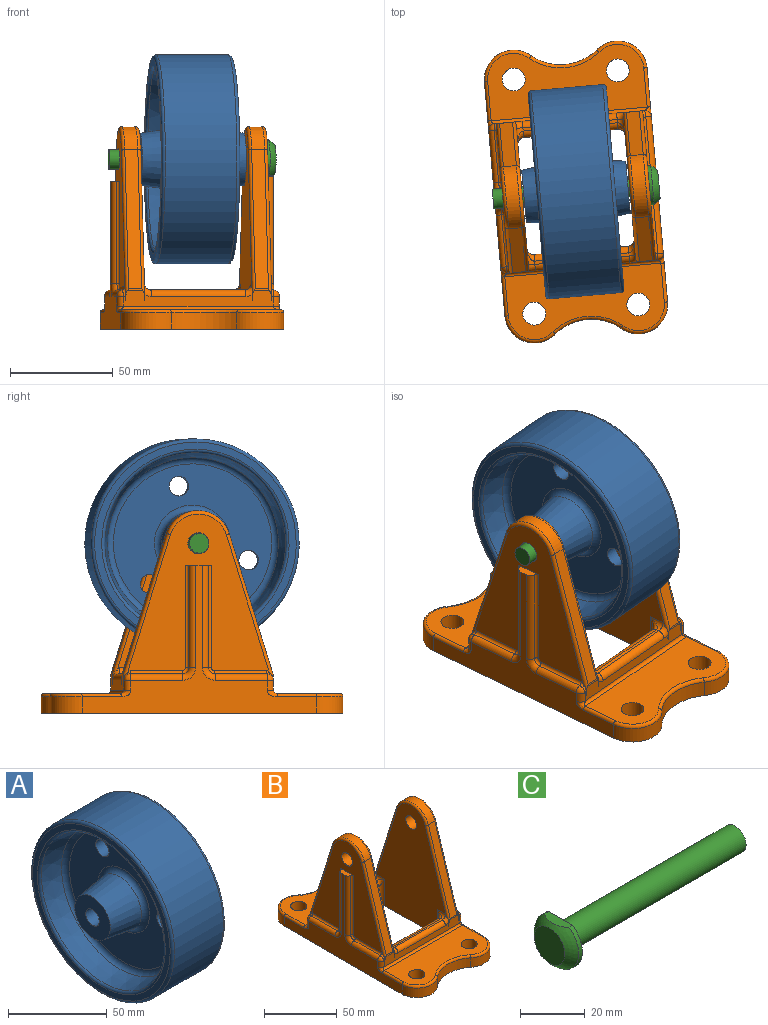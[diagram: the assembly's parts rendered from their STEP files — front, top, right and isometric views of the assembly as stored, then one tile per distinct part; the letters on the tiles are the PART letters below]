
ASSEMBLY  parts=3 mates=2
PART A: 23 faces, bbox 50.8x110x110 mm
  f0: cone r=15.49mm half-angle=8.1deg, axis (-1,0,0), area 1744.1mm2, adj f1,f19
  f1: torus R=18.63mm, axis (1,0,0), area 476.6mm2, adj f0,f2
  f2: plane 77.34x77.34mm, normal (1,0,0), area 3394.4mm2, adj f1,f3,f20,f21,f22
  f3: torus R=38.67mm, axis (1,0,0), area 1110.5mm2, adj f2,f4
  f4: cone r=44.19mm half-angle=11.3deg, axis (1,0,0), area 3318.4mm2, adj f3,f5
  f5: torus R=45.75mm, axis (1,0,0), area 614mm2, adj f4,f6
  f6: plane 98.43x98.43mm, normal (1,0,0), area 1032.6mm2, adj f5,f7
  f7: torus R=49.21mm, axis (1,0,0), area 786.9mm2, adj f6,f8
  f8: cylinder r=50.8mm len=101.6mm, axis (1,0,0), area 11147.6mm2, adj f7,f9
  f9: torus R=49.21mm, axis (1,0,0), area 786.9mm2, adj f8,f10
  f10: plane 98.43x98.43mm, normal (-1,0,0), area 1032.6mm2, adj f9,f11
  f11: torus R=45.75mm, axis (1,0,0), area 614mm2, adj f10,f12
  f12: cone r=44.19mm half-angle=11.3deg, axis (-1,0,0), area 3318.4mm2, adj f11,f13
  f13: torus R=38.67mm, axis (1,0,0), area 1110.5mm2, adj f12,f14
  f14: plane 77.34x77.34mm, normal (-1,0,0), area 3394.4mm2, adj f13,f15,f20,f21,f22
  f15: torus R=18.63mm, axis (1,0,0), area 476.6mm2, adj f14,f16
  f16: cone r=15.49mm half-angle=8.1deg, axis (1,0,0), area 1744.1mm2, adj f15,f17
  f17: plane 25.4x25.4mm, normal (-1,0,0), area 433.5mm2, adj f16,f18
  f18: cylinder r=4.83mm len=50.8mm, axis (1,0,0), area 1540.4mm2, adj f17,f19
  f19: plane 25.4x25.4mm, normal (1,0,0), area 433.5mm2, adj f0,f18
  f20: cylinder r=4.76mm len=9.53mm, axis (-1,0,0), area 190mm2, adj f2,f14
  f21: cylinder r=4.76mm len=9.53mm, axis (-1,0,0), area 190mm2, adj f2,f14
  f22: cylinder r=4.76mm len=9.53mm, axis (-1,0,0), area 190mm2, adj f2,f14
PART B: 131 faces, bbox 82.6x146.1x100.6 mm
  f0: cylinder r=1.59mm len=49.76mm, axis (0,0,-1), area 110.8mm2, adj f24,f89,f101,f130
  f1: cylinder r=1.59mm len=49.76mm, axis (0,0,1), area 110.8mm2, adj f24,f91,f102,f130
  f2: plane 114.87x72.55mm, normal (-1,0,0), area 1649.1mm2, adj f10,f16,f18,f50,f56,f99,f100,f101
  f3: plane 114.87x74.94mm, normal (1,0,0), area 1657mm2, adj f10,f12,f22,f52,f59,f81,f96,f97
  f4: plane 76.21x68.34mm, normal (1,0,0), area 2608.7mm2, adj f43,f44,f45,f46,f81,f86,f87,f88
  f5: plane 7.72x2.42mm, normal (1,0,0), area 5.4mm2, adj f8,f49,f127
  f6: plane 7.72x2.42mm, normal (-1,0,0), area 5.4mm2, adj f8,f32,f129
  f7: plane 46.04x15.88mm, normal (0,-1,0), area 730.8mm2, adj f10,f61,f66,f73
  f8: plane 73.91x8.33mm, normal (0,1,0), area 396mm2, adj f5,f6,f32,f35,f46,f49,f76,f78
  f9: plane 46.04x1.59mm, normal (0,0,1), area 73.1mm2, adj f62,f65,f73,f128
  f10: plane 142.88x79.38mm, normal (0,0,-1), area 7276.6mm2, adj f2,f3,f7,f11,f12,f13,f14,f15
  f11: plane 96.84x67.46mm, normal (-1,0,0), area 4313.3mm2, adj f10,f43,f47,f48,f49,f61,f62,f67
  f12: cylinder r=14.29mm len=23.7mm, axis (0,0,-1), area 259.7mm2, adj f3,f10,f13,f21
  f13: cylinder r=25.4mm len=31.97mm, axis (0,0,-1), area 274.4mm2, adj f10,f12,f16,f20
  f14: cylinder r=5.56mm len=11.11mm, axis (0,0,-1), area 332.5mm2, adj f10,f17
  f15: cylinder r=5.56mm len=11.11mm, axis (0,0,-1), area 332.5mm2, adj f10,f17
  f16: cylinder r=14.29mm len=23.7mm, axis (0,0,-1), area 259.7mm2, adj f2,f10,f13,f19
  f17: plane 76.2x31.75mm, normal (0,0,1), area 1891.4mm2, adj f14,f15,f18,f19,f20,f21,f22,f85
  f18: cylinder r=1.59mm len=19.05mm, axis (0,1,0), area 47.5mm2, adj f2,f17,f19,f111
  f19: torus R=12.7mm, axis (0,0,1), area 78.3mm2, adj f16,f17,f18,f20
  f20: torus R=26.99mm, axis (0,0,1), area 88.3mm2, adj f13,f17,f19,f21
  f21: torus R=12.7mm, axis (0,0,1), area 78.3mm2, adj f12,f17,f20,f22
  f22: cylinder r=1.59mm len=19.05mm, axis (0,-1,0), area 47.5mm2, adj f3,f17,f21,f123
  f23: plane 96.84x67.46mm, normal (1,0,0), area 4313.3mm2, adj f10,f29,f30,f31,f32,f63,f64,f65
  f24: plane 76.21x68.34mm, normal (-1,0,0), area 2639mm2, adj f0,f1,f29,f33,f34,f35,f89,f90
  f25: plane 73.91x8.33mm, normal (0,-1,0), area 396mm2, adj f30,f33,f36,f37,f44,f47,f75,f77
  f26: plane 67.78x21.22mm, normal (0,-0.95,0.3), area 451mm2, adj f27,f30,f33,f75
  f27: cylinder r=15.88mm len=30.3mm, axis (-1,0,0), area 255.5mm2, adj f26,f28,f31,f34
  f28: plane 67.78x21.22mm, normal (0,0.95,0.3), area 451mm2, adj f27,f32,f35,f76
  f29: cylinder r=5.16mm len=10.32mm, axis (-1,0,0), area 308.8mm2, adj f23,f24
  f30: cylinder r=1.59mm len=73.62mm, axis (0,-0.3,-0.95), area 183.5mm2, adj f23,f25,f26,f31,f37,f75,f126
  f31: torus R=14.29mm, axis (-1,0,0), area 96.7mm2, adj f23,f27,f30,f32
  f32: cylinder r=1.59mm len=73.62mm, axis (0,-0.3,0.95), area 183.5mm2, adj f6,f8,f23,f28,f31,f76,f129
  f33: cylinder r=1.59mm len=73.68mm, axis (0,-0.3,-0.95), area 183.8mm2, adj f24,f25,f26,f34,f75,f83,f116
  f34: torus R=14.29mm, axis (1,0,0), area 96.7mm2, adj f24,f27,f33,f35
  f35: cylinder r=1.59mm len=73.68mm, axis (0,-0.3,0.95), area 183.8mm2, adj f8,f24,f28,f34,f76,f82,f108
  f36: plane 7.72x2.42mm, normal (1,0,0), area 5.4mm2, adj f25,f47,f124
  f37: plane 7.72x2.42mm, normal (-1,0,0), area 5.4mm2, adj f25,f30,f126
  f38: plane 46.04x15.88mm, normal (0,1,0), area 730.8mm2, adj f10,f63,f68,f70
  f39: plane 46.04x1.59mm, normal (0,0,1), area 73.1mm2, adj f64,f67,f70,f125
  f40: plane 67.78x21.22mm, normal (0,-0.95,0.3), area 451mm2, adj f41,f44,f47,f77
  f41: cylinder r=15.88mm len=30.3mm, axis (-1,0,0), area 255.5mm2, adj f40,f42,f45,f48
  f42: plane 67.78x21.22mm, normal (0,0.95,0.3), area 451mm2, adj f41,f46,f49,f78
  f43: cylinder r=5.16mm len=10.32mm, axis (-1,0,0), area 308.8mm2, adj f4,f11
  f44: cylinder r=1.59mm len=73.68mm, axis (0,-0.3,-0.95), area 183.8mm2, adj f4,f25,f40,f45,f77,f80,f112
  f45: torus R=14.29mm, axis (-1,0,0), area 96.7mm2, adj f4,f41,f44,f46
  f46: cylinder r=1.59mm len=73.68mm, axis (0,-0.3,0.95), area 183.8mm2, adj f4,f8,f42,f45,f78,f79,f120
  f47: cylinder r=1.59mm len=73.62mm, axis (0,0.3,0.95), area 183.5mm2, adj f11,f25,f36,f40,f48,f77,f124
  f48: torus R=14.29mm, axis (1,0,0), area 96.7mm2, adj f11,f41,f47,f49
  f49: cylinder r=1.59mm len=73.62mm, axis (0,0.3,-0.95), area 183.5mm2, adj f5,f8,f11,f42,f48,f78,f127
  f50: cylinder r=14.29mm len=23.7mm, axis (0,0,-1), area 259.7mm2, adj f2,f10,f51,f57
  f51: cylinder r=25.4mm len=31.97mm, axis (0,0,-1), area 274.4mm2, adj f10,f50,f52,f58
  f52: cylinder r=14.29mm len=23.7mm, axis (0,0,-1), area 259.7mm2, adj f3,f10,f51,f60
  f53: cylinder r=5.56mm len=11.11mm, axis (0,0,-1), area 332.5mm2, adj f10,f55
  f54: cylinder r=5.56mm len=11.11mm, axis (0,0,-1), area 332.5mm2, adj f10,f55
  f55: plane 76.2x31.75mm, normal (0,0,1), area 1891.4mm2, adj f53,f54,f56,f57,f58,f59,f60,f84
  f56: cylinder r=1.59mm len=19.05mm, axis (0,1,0), area 47.5mm2, adj f2,f55,f57,f119
  f57: torus R=12.7mm, axis (0,0,1), area 78.3mm2, adj f50,f55,f56,f58
  f58: torus R=26.99mm, axis (0,0,1), area 88.3mm2, adj f51,f55,f57,f60
  f59: cylinder r=1.59mm len=19.05mm, axis (0,-1,0), area 47.5mm2, adj f3,f55,f60,f115
  f60: torus R=12.7mm, axis (0,0,1), area 78.3mm2, adj f52,f55,f58,f59
  f61: cylinder r=3.17mm len=22.23mm, axis (0,0,-1), area 95mm2, adj f7,f10,f11,f74
  f62: cylinder r=3.17mm len=7.94mm, axis (0,-1,0), area 19.4mm2, adj f9,f11,f74,f127
  f63: cylinder r=3.17mm len=22.23mm, axis (0,0,1), area 95mm2, adj f10,f23,f38,f69
  f64: cylinder r=3.17mm len=7.94mm, axis (0,1,0), area 19.4mm2, adj f23,f39,f69,f126
  f65: cylinder r=3.17mm len=7.94mm, axis (0,1,0), area 19.4mm2, adj f9,f23,f72,f129
  f66: cylinder r=3.17mm len=22.23mm, axis (0,0,-1), area 95mm2, adj f7,f10,f23,f72
  f67: cylinder r=3.17mm len=7.94mm, axis (0,-1,0), area 19.4mm2, adj f11,f39,f71,f124
  f68: cylinder r=3.17mm len=22.23mm, axis (0,0,1), area 95mm2, adj f10,f11,f38,f71
  f69: bspline ~6.35x6.35mm, area 10.6mm2, adj f63,f64,f70
  f70: cylinder r=3.17mm len=46.04mm, axis (1,0,0), area 229.6mm2, adj f38,f39,f69,f71
  f71: bspline ~6.35x6.35mm, area 10.6mm2, adj f67,f68,f70
  f72: bspline ~6.35x6.35mm, area 10.6mm2, adj f65,f66,f73
  f73: cylinder r=3.17mm len=46.04mm, axis (-1,0,0), area 229.6mm2, adj f7,f9,f72,f74
  f74: bspline ~6.35x6.35mm, area 10.6mm2, adj f61,f62,f73
  f75: cylinder r=3.17mm len=7.68mm, axis (-1,0,0), area 6.8mm2, adj f25,f26,f30,f33
  f76: cylinder r=3.17mm len=7.68mm, axis (-1,0,0), area 6.8mm2, adj f8,f28,f32,f35
  f77: cylinder r=3.17mm len=7.68mm, axis (-1,0,0), area 6.8mm2, adj f25,f40,f44,f47
  f78: cylinder r=3.17mm len=7.68mm, axis (-1,0,0), area 6.8mm2, adj f8,f42,f46,f49
  f79: plane 6.62x2.56mm, normal (-1,0,0), area 3.4mm2, adj f8,f46,f120
  f80: plane 6.62x2.57mm, normal (-1,0,0), area 3.4mm2, adj f25,f44,f112
  f81: plane 12.7x3.97mm, normal (0,0,1), area 34.9mm2, adj f3,f4,f86,f93,f98,f105
  f82: plane 6.62x2.57mm, normal (1,0,0), area 3.4mm2, adj f8,f35,f108
  f83: plane 6.62x2.56mm, normal (1,0,0), area 3.4mm2, adj f25,f33,f116
  f84: cylinder r=1.59mm len=76.2mm, axis (1,0,0), area 186.1mm2, adj f25,f55,f115,f119
  f85: cylinder r=1.59mm len=76.2mm, axis (-1,0,0), area 186.1mm2, adj f8,f17,f111,f123
  f86: cylinder r=1.59mm len=52.14mm, axis (0,0,-1), area 116.2mm2, adj f4,f81,f87,f98
  f87: torus R=1.59mm, axis (-1,0,0), area 8.9mm2, adj f4,f86,f88,f97
  f88: cylinder r=1.59mm len=25.4mm, axis (0,-1,0), area 56.6mm2, adj f4,f87,f96,f112
  f89: torus R=1.59mm, axis (1,0,0), area 8.9mm2, adj f0,f24,f90,f100
  f90: cylinder r=1.59mm len=25.4mm, axis (0,-1,0), area 56.6mm2, adj f24,f89,f99,f116
  f91: torus R=1.59mm, axis (1,0,0), area 8.9mm2, adj f1,f24,f92,f103
  f92: cylinder r=1.59mm len=25.4mm, axis (0,-1,0), area 56.6mm2, adj f24,f91,f104,f108
  f93: cylinder r=1.59mm len=52.14mm, axis (0,0,1), area 116.2mm2, adj f4,f81,f94,f105
  f94: torus R=1.59mm, axis (-1,0,0), area 8.9mm2, adj f4,f93,f95,f106
  f95: cylinder r=1.59mm len=25.4mm, axis (0,-1,0), area 56.6mm2, adj f4,f94,f107,f120
  f96: cylinder r=3.17mm len=25.4mm, axis (0,-1,0), area 113.2mm2, adj f3,f88,f97,f113
  f97: torus R=6.28mm, axis (1,0,0), area 30.8mm2, adj f3,f87,f96,f98
  f98: cylinder r=3.17mm len=52.14mm, axis (0,0,-1), area 232.3mm2, adj f3,f81,f86,f97
  f99: cylinder r=3.17mm len=25.4mm, axis (0,-1,0), area 113.2mm2, adj f2,f90,f100,f117
  f100: torus R=6.28mm, axis (1,0,0), area 30.8mm2, adj f2,f89,f99,f101
  f101: cylinder r=3.17mm len=49.76mm, axis (0,0,-1), area 221.7mm2, adj f0,f2,f100,f130
  f102: cylinder r=3.17mm len=49.76mm, axis (0,0,1), area 221.7mm2, adj f1,f2,f103,f130
  f103: torus R=6.28mm, axis (1,0,0), area 30.8mm2, adj f2,f91,f102,f104
  f104: cylinder r=3.17mm len=25.4mm, axis (0,-1,0), area 113.2mm2, adj f2,f92,f103,f109
  f105: cylinder r=3.17mm len=52.14mm, axis (0,0,1), area 232.3mm2, adj f3,f81,f93,f106
  f106: torus R=6.28mm, axis (1,0,0), area 30.8mm2, adj f3,f94,f105,f107
  f107: cylinder r=3.17mm len=25.4mm, axis (0,-1,0), area 113.2mm2, adj f3,f95,f106,f121
  f108: torus R=4.76mm, axis (0,1,0), area 8mm2, adj f8,f24,f35,f82,f92,f109
  f109: sphere r=3.17mm, area 14.1mm2, adj f104,f108,f110
  f110: cylinder r=3.17mm len=4.83mm, axis (0,0,-1), area 24.1mm2, adj f2,f8,f109,f111
  f111: bspline ~4.76x3.18mm, area 14.4mm2, adj f2,f18,f85,f110
  f112: torus R=4.76mm, axis (0,1,0), area 8mm2, adj f4,f25,f44,f80,f88,f113
  f113: sphere r=3.17mm, area 9mm2, adj f96,f112,f114
  f114: cylinder r=3.17mm len=4.83mm, axis (0,0,1), area 24.1mm2, adj f3,f25,f113,f115
  f115: bspline ~4.76x3.18mm, area 14.4mm2, adj f3,f59,f84,f114
  f116: torus R=4.76mm, axis (0,1,0), area 8mm2, adj f24,f25,f33,f83,f90,f117
  f117: sphere r=3.17mm, area 14.1mm2, adj f99,f116,f118
  f118: cylinder r=3.17mm len=4.83mm, axis (0,0,-1), area 24.1mm2, adj f2,f25,f117,f119
  f119: bspline ~4.76x3.18mm, area 14.4mm2, adj f2,f56,f84,f118
  f120: torus R=4.76mm, axis (0,1,0), area 8mm2, adj f4,f8,f46,f79,f95,f121
  f121: sphere r=3.17mm, area 9mm2, adj f107,f120,f122
  f122: cylinder r=3.17mm len=4.83mm, axis (0,0,1), area 24.1mm2, adj f3,f8,f121,f123
  f123: bspline ~4.76x3.18mm, area 14.4mm2, adj f3,f22,f85,f122
  f124: torus R=6.35mm, axis (0,1,0), area 19.1mm2, adj f11,f25,f36,f47,f67,f125
  f125: cylinder r=3.17mm len=46.04mm, axis (-1,0,0), area 229.6mm2, adj f25,f39,f124,f126
  f126: torus R=6.35mm, axis (0,1,0), area 19.1mm2, adj f23,f25,f30,f37,f64,f125
  f127: torus R=6.35mm, axis (0,1,0), area 19.1mm2, adj f5,f8,f11,f49,f62,f128
  f128: cylinder r=3.17mm len=46.04mm, axis (1,0,0), area 229.6mm2, adj f8,f9,f127,f129
  f129: torus R=6.35mm, axis (0,1,0), area 19.1mm2, adj f6,f8,f23,f32,f65,f128
  f130: plane 12.7x3.97mm, normal (0,0,1), area 34.9mm2, adj f0,f1,f2,f24,f101,f102
PART C: 7 faces, bbox 81x19.1x19.1 mm
  f0: cylinder r=9.53mm len=19.05mm, axis (-1,0,0), area 77.3mm2, adj f1,f2,f5
  f1: plane 10.53x3.64mm, normal (0,0,1), area 31.6mm2, adj f0,f2,f5
  f2: plane 19.05x17.46mm, normal (1,0,0), area 202.4mm2, adj f0,f1,f3
  f3: cylinder r=4.76mm len=76.2mm, axis (-1,0,0), area 2280.2mm2, adj f2,f4
  f4: plane 9.53x9.53mm, normal (1,0,0), area 71.3mm2, adj f3
  f5: sphere r=11.11mm, area 202.5mm2, adj f0,f1,f6
  f6: plane 13.31x13.31mm, normal (-1,0,0), area 139.2mm2, adj f5
PLACE A rot(axis=(0.02,-0.39,-0.92),175.4deg) t=(-16.07,-61.91,93.52)mm
PLACE B rot(axis=(0,0,1),5deg) t=(142.9,-52.73,10.97)mm fixed
PLACE C rot(axis=(0.04,-1,0),180deg) t=(24.26,-58.38,169.72)mm
MATE fastened C.f0 <-> B.f27  axis (-1,-0.09,0) through (-56.4,-65.44,93.52)mm
MATE revolute A.f0 <-> C.f0  axis (-1,-0.09,0) through (-16.07,-61.91,93.52)mm
